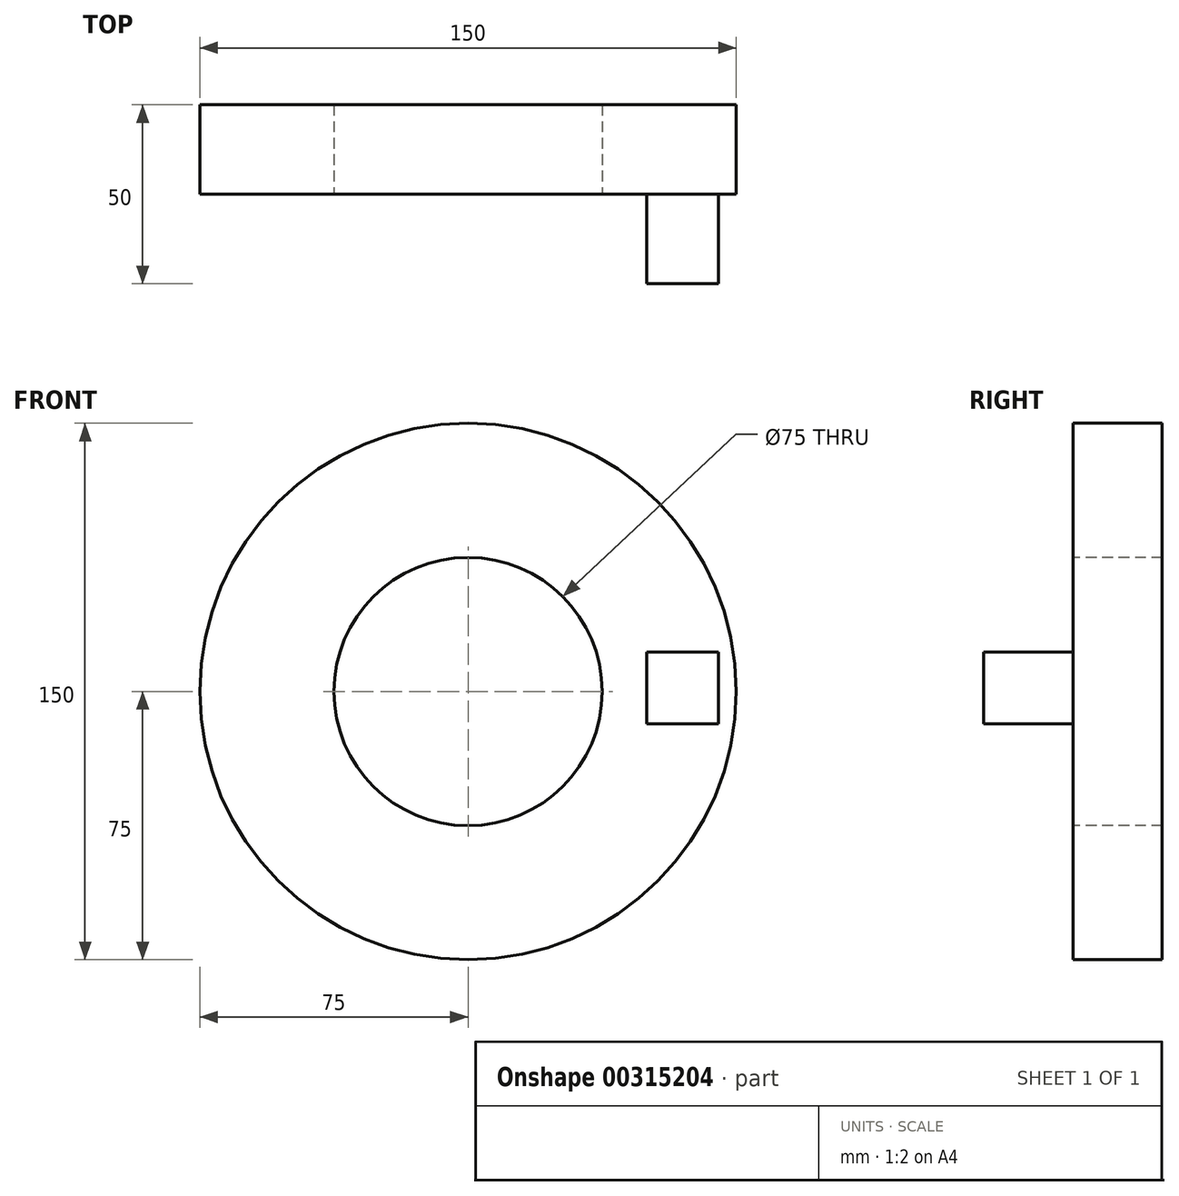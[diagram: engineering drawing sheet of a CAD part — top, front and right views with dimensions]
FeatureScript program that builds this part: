
annotation { "Feature Type Name" : "Feature", "Feature Type Description" : "" }
export const myFeature = defineFeature(function(context is Context, id is Id, definition is map)
    precondition{}
    {
        {
            var Q0;
            Q0=qCreatedBy(makeId("Front.planeOp"),FACE);
            var sketch = newSketch(context, id + "F0", { "sketchPlane" : qUnion([Q0])});
            skCircle(sketch, "E0", {"center": v(0, 0) * mm, "radius": 75 * mm});
            skSolve(sketch);
        }
        {
            var Q0;
            Q0=makeQuery(id+"F0.imprint","IMPRINT",FACE,{"disambiguationData":[TD([[makeQuery(id+"F0.imprint","IMPRINT",EDGE,{"derivedFrom":sQuery(id+"F0.wireOp",EDGE,"E0")}),1.0]])]});
            extrude(context, id + "F1", {"entities" : qUnion([Q0]), "depth" : 25 * mm});
        }
        {
            var Q0;
            Q0=makeQuery(id+"F1.opExtrude","CAP_FACE",FACE,{"disambiguationData":[OSD([sQuery(id+"F0.wireOp",EDGE,"E0")])],"isStart":false});
            var sketch = newSketch(context, id + "F2", { "sketchPlane" : qUnion([Q0])});
            skCircle(sketch, "E1", {"center": v(0, 0) * mm, "radius": 37.5 * mm});
            skSolve(sketch);
        }
        {
            var Q0;
            Q0 = qSketchRegion(id + "F2", true);
            extrude(context, id + "F3", {"entities" : qUnion([Q0]), "operationType" : NewBodyOperationType.REMOVE, "oppositeDirection" : true, "depth" : 25 * mm});
        }
        {
            var Q0;
            Q0=makeQuery(id+"F1.opExtrude","CAP_FACE",FACE,{"disambiguationData":[OSD([sQuery(id+"F0.wireOp",EDGE,"E0")])],"isStart":false});
            var sketch = newSketch(context, id + "F4", { "sketchPlane" : qUnion([Q0])});
            skLineSegment(sketch, "E2.bottom", {"start": v(70, -9.03) * mm, "end": v(50, -9.03) * mm});
            skLineSegment(sketch, "E2.top", {"start": v(70, 10.97) * mm, "end": v(50, 10.97) * mm});
            skLineSegment(sketch, "E2.left", {"start": v(70, -9.03) * mm, "end": v(70, 10.97) * mm});
            skLineSegment(sketch, "E2.right", {"start": v(50, -9.03) * mm, "end": v(50, 10.97) * mm});
            skPoint(sketch, "E2.middle", {"position": v(60, 0.97) * mm});
            skSolve(sketch);
        }
        {
            var Q0;
            Q0=makeQuery(id+"F4.imprint","IMPRINT",FACE,{"disambiguationData":[TD([[makeQuery(id+"F4.imprint","IMPRINT",EDGE,{"derivedFrom":sQuery(id+"F4.wireOp",EDGE,"E2.bottom")}),-1.0]])]});
            extrude(context, id + "F5", {"entities" : qUnion([Q0]), "operationType" : NewBodyOperationType.ADD, "depth" : 25 * mm});
        }
    });
